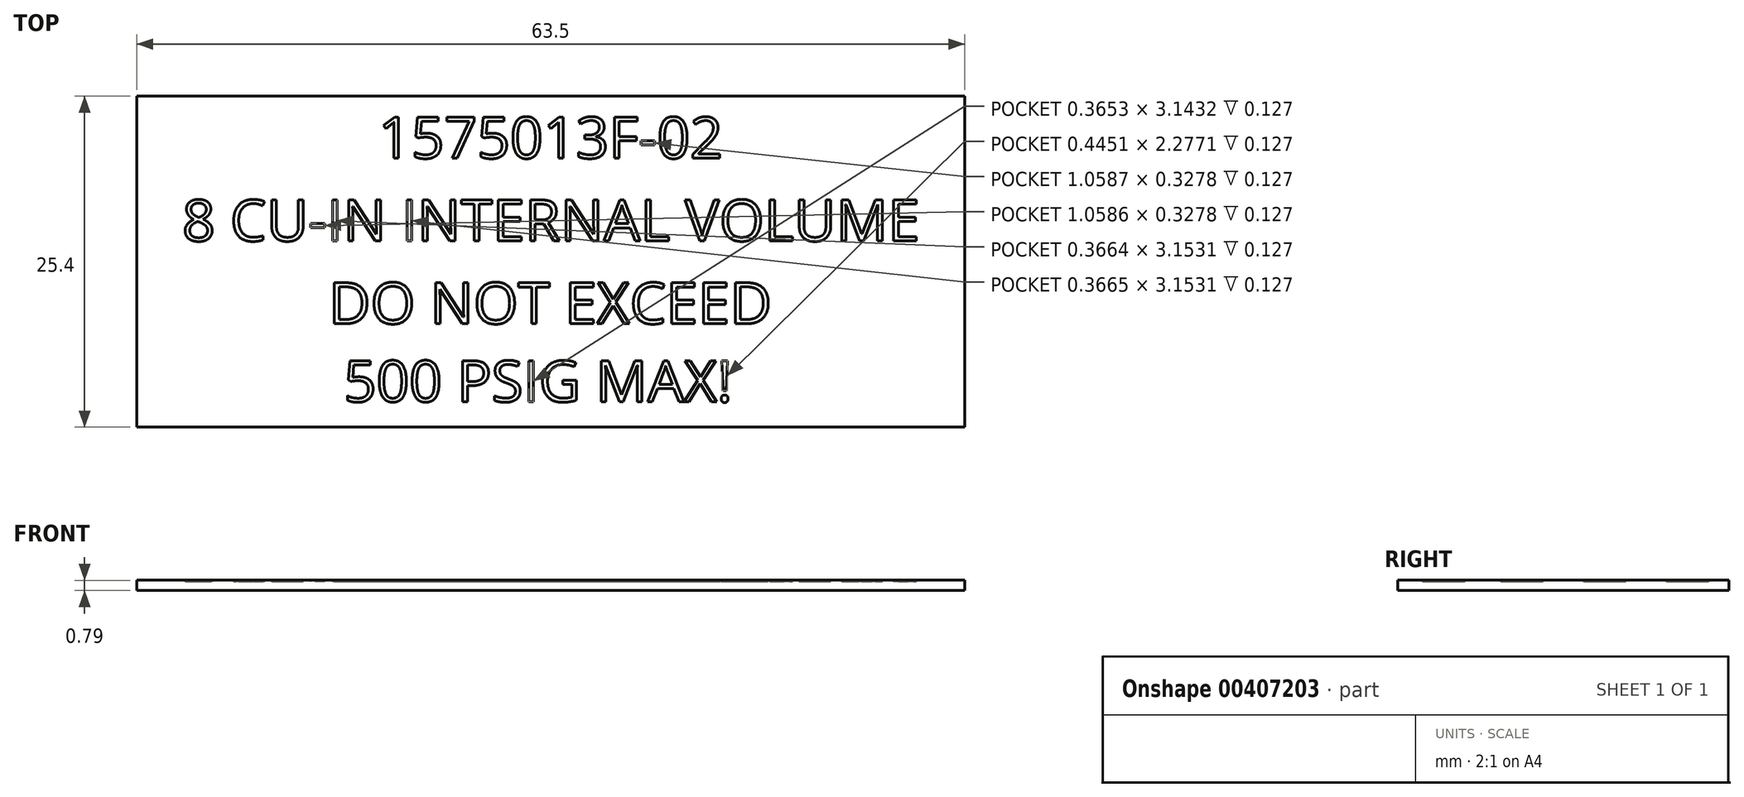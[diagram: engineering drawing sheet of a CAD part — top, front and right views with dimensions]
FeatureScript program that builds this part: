
annotation { "Feature Type Name" : "Feature", "Feature Type Description" : "" }
export const myFeature = defineFeature(function(context is Context, id is Id, definition is map)
    precondition{}
    {
        {
            var Q0;
            Q0=qCreatedBy(makeId("Top.planeOp"),FACE);
            var sketch = newSketch(context, id + "F0", { "sketchPlane" : qUnion([Q0])});
            skLineSegment(sketch, "E0.bottom", {"start": v(31.75, 12.7) * mm, "end": v(-31.75, 12.7) * mm});
            skLineSegment(sketch, "E0.top", {"start": v(31.75, -12.7) * mm, "end": v(-31.75, -12.7) * mm});
            skLineSegment(sketch, "E0.left", {"start": v(31.75, 12.7) * mm, "end": v(31.75, -12.7) * mm});
            skLineSegment(sketch, "E0.right", {"start": v(-31.75, 12.7) * mm, "end": v(-31.75, -12.7) * mm});
            skPoint(sketch, "E0.middle", {"position": v(0, 0) * mm});
            skSolve(sketch);
        }
        {
            var Q0;
            Q0 = qSketchRegion(id + "F0", true);
            extrude(context, id + "F1", {"entities" : qUnion([Q0]), "depth" : 0.8 * mm});
        }
        {
            var Q0;
            Q0=makeQuery(id+"F1.opExtrude","CAP_FACE",FACE,{"disambiguationData":[OSD([sQuery(id+"F0.wireOp",EDGE,"E0.bottom"),sQuery(id+"F0.wireOp",EDGE,"E0.top"),sQuery(id+"F0.wireOp",EDGE,"E0.left"),sQuery(id+"F0.wireOp",EDGE,"E0.right")])],"isStart":false});
            var sketch = newSketch(context, id + "F2", { "sketchPlane" : qUnion([Q0])});
            skText(sketch, "E1", { "text": "1575013F-02\n", "fontName": "OpenSans-Regular.ttf"});
            skText(sketch, "E2", { "text": "8 CU-IN INTERNAL VOLUME", "fontName": "OpenSans-Regular.ttf"});
            skPoint(sketch, "E3", {"position": v(0, 9.53) * mm});
            skPoint(sketch, "E4", {"position": v(0, 3.17) * mm});
            skText(sketch, "E5", { "text": "DO NOT EXCEED\n 500 PSIG MAX!", "fontName": "OpenSans-Regular.ttf"});
            skPoint(sketch, "E6", {"position": v(0, -3.18) * mm});
            const initialGuessF2  = {"E1": [-0.01322, 0.00794, 1, 0, 0.00318], "E2": [-0.02826, 0.00159, 1, 0, 0.00318], "E5": [-0.01703, -0.00476, 1, 0, 0.00317]};
            skSetInitialGuess(sketch, initialGuessF2);
            skSolve(sketch);
        }
        {
            var Q0;
            Q0 = qSketchRegion(id + "F2", true);
            extrude(context, id + "F3", {"entities" : qUnion([Q0]), "operationType" : NewBodyOperationType.REMOVE, "oppositeDirection" : true, "depth" : 0.13 * mm});
        }
    });
